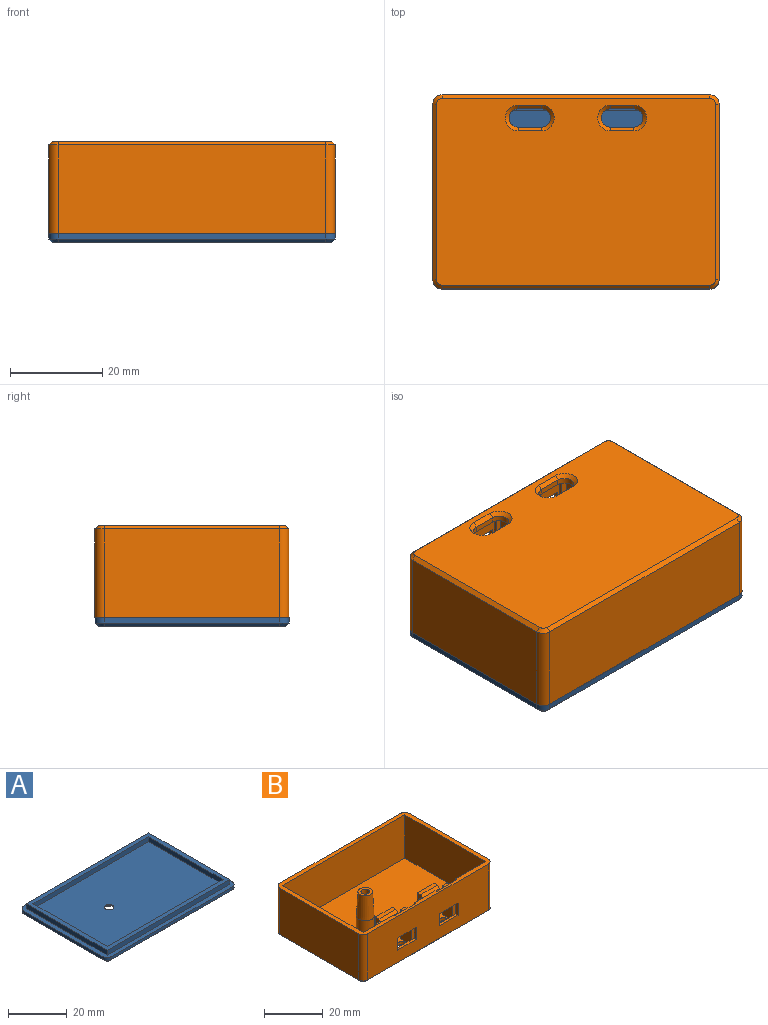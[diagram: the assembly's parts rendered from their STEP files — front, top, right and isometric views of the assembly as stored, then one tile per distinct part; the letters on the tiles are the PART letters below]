
ASSEMBLY  parts=2 mates=1
PART A: 30 faces, bbox 62x42x4 mm
  f0: plane 62x42mm, normal (0,0,1), area 323mm2, adj f1,f2,f3,f4,f6,f7,f8,f9
  f1: plane 38x1.2mm, normal (1,0,0), area 45.6mm2, adj f0,f6,f9,f25
  f2: plane 58x1.2mm, normal (0,1,0), area 69.6mm2, adj f0,f6,f7,f29
  f3: plane 38x1.2mm, normal (-1,0,0), area 45.6mm2, adj f0,f7,f8,f26
  f4: plane 58x1.2mm, normal (0,-1,0), area 69.6mm2, adj f0,f8,f9,f22
  f5: plane 60.4x40.4mm, normal (0,0,-1), area 2402.6mm2, adj f21,f22,f23,f24,f25,f26,f27,f28
  f6: cylinder r=2mm len=2mm, axis (0,0,1), area 3.8mm2, adj f0,f1,f2,f27
  f7: cylinder r=2mm len=2mm, axis (0,0,-1), area 3.8mm2, adj f0,f2,f3,f28
  f8: cylinder r=2mm len=2mm, axis (0,0,1), area 3.8mm2, adj f0,f3,f4,f24
  f9: cylinder r=2mm len=2mm, axis (0,0,-1), area 3.8mm2, adj f0,f1,f4,f23
  f10: plane 58.76x2mm, normal (0,-1,0), area 117.5mm2, adj f0,f11,f17,f18
  f11: plane 38.76x2mm, normal (1,0,0), area 77.5mm2, adj f0,f10,f12,f18
  f12: plane 58.76x2mm, normal (0,1,0), area 117.5mm2, adj f0,f11,f17,f18
  f13: plane 35.56x2mm, normal (-1,0,0), area 71.1mm2, adj f14,f16,f18,f19
  f14: plane 55.56x2mm, normal (0,1,0), area 111.1mm2, adj f13,f15,f18,f19
  f15: plane 35.56x2mm, normal (1,0,0), area 71.1mm2, adj f14,f16,f18,f19
  f16: plane 55.56x2mm, normal (0,-1,0), area 111.1mm2, adj f13,f15,f18,f19
  f17: plane 38.76x2mm, normal (-1,0,0), area 77.5mm2, adj f0,f10,f12,f18
  f18: plane 58.76x38.76mm, normal (0,0,1), area 301.8mm2, adj f10,f11,f12,f13,f14,f15,f16,f17
  f19: plane 55.56x35.56mm, normal (0,0,1), area 1967.7mm2, adj f13,f14,f15,f16,f20
  f20: cylinder r=1.6mm len=3.2mm, axis (0,0,1), area 2mm2, adj f19,f21
  f21: cone r=1.6mm half-angle=45deg, axis (0,0,-1), area 40mm2, adj f5,f20
  f22: plane 58x0.8mm, normal (0,-0.71,-0.71), area 65.6mm2, adj f4,f5,f23,f24
  f23: cone r=1.2mm half-angle=45deg, axis (0,0,1), area 2.8mm2, adj f5,f9,f22,f25
  f24: cone r=1.2mm half-angle=45deg, axis (0,0,1), area 2.8mm2, adj f5,f8,f22,f26
  f25: plane 38x0.8mm, normal (0.71,0,-0.71), area 43mm2, adj f1,f5,f23,f27
  f26: plane 38x0.8mm, normal (-0.71,0,-0.71), area 43mm2, adj f3,f5,f24,f28
  f27: cone r=1.2mm half-angle=45deg, axis (0,0,1), area 2.8mm2, adj f5,f6,f25,f29
  f28: cone r=1.2mm half-angle=45deg, axis (0,0,1), area 2.8mm2, adj f5,f7,f26,f29
  f29: plane 58x0.8mm, normal (0,0.71,-0.71), area 65.6mm2, adj f2,f5,f27,f28
PART B: 96 faces, bbox 62x42x20 mm
  f0: plane 10.1x8mm, normal (0,-1,0), area 80.8mm2, adj f20,f55,f58,f68
  f1: plane 10.1x8mm, normal (0,-1,0), area 80.8mm2, adj f20,f61,f63,f66
  f2: plane 12x5mm, normal (1,0,0), area 60mm2, adj f20,f26,f60,f62
  f3: plane 12x5mm, normal (-1,0,0), area 60mm2, adj f9,f20,f64,f65
  f4: plane 12x5mm, normal (1,0,0), area 60mm2, adj f20,f28,f54,f56
  f5: plane 12x5mm, normal (-1,0,0), area 60mm2, adj f14,f20,f57,f59
  f6: plane 12x5mm, normal (1,0,0), area 60mm2, adj f9,f20,f64,f65
  f7: plane 18x0.6mm, normal (1,0,0), area 10.8mm2, adj f18,f20,f21,f78
  f8: plane 18x0.6mm, normal (-1,0,0), area 10.8mm2, adj f18,f20,f21,f79
  f9: plane 5x2mm, normal (0,0,1), area 10mm2, adj f3,f6,f64,f65
  f10: plane 8x1.6mm, normal (0,0,1), area 12.8mm2, adj f61,f63,f71,f72
  f11: plane 12x5mm, normal (1,0,0), area 60mm2, adj f14,f20,f57,f59
  f12: plane 18x0.6mm, normal (1,0,0), area 10.8mm2, adj f17,f20,f21,f79
  f13: plane 18x0.6mm, normal (-1,0,0), area 10.8mm2, adj f17,f20,f21,f77
  f14: plane 5x2mm, normal (0,0,1), area 10mm2, adj f5,f11,f57,f59
  f15: plane 8x1.6mm, normal (0,0,1), area 12.8mm2, adj f55,f58,f70,f73
  f16: plane 58x19.2mm, normal (0,-1,0), area 1023.6mm2, adj f21,f37,f38,f39,f40,f41,f42,f43
  f17: plane 18x10mm, normal (0,1,0), area 135mm2, adj f12,f13,f20,f21,f41,f42,f43,f44
  f18: plane 18x10mm, normal (0,1,0), area 135mm2, adj f7,f8,f20,f21,f37,f38,f39,f40
  f19: plane 60.4x40.4mm, normal (0,0,-1), area 2333.7mm2, adj f80,f81,f82,f83,f84,f85,f86,f87
  f20: plane 58.8x39.4mm, normal (0,0,1), area 2118.4mm2, adj f0,f1,f2,f3,f4,f5,f6,f7
  f21: plane 62x42mm, normal (0,0,1), area 307.1mm2, adj f7,f8,f12,f13,f16,f17,f18,f22
  f22: plane 38x19.2mm, normal (1,0,0), area 729.6mm2, adj f21,f50,f51,f80
  f23: plane 58x19.2mm, normal (0,1,0), area 1113.6mm2, adj f21,f51,f52,f84
  f24: plane 38x19.2mm, normal (-1,0,0), area 729.6mm2, adj f21,f52,f53,f87
  f25: plane 12x5mm, normal (-1,0,0), area 60mm2, adj f20,f26,f60,f62
  f26: plane 5x2mm, normal (0,0,1), area 10mm2, adj f2,f25,f60,f62
  f27: plane 12x5mm, normal (-1,0,0), area 60mm2, adj f20,f28,f54,f56
  f28: plane 5x2mm, normal (0,0,1), area 10mm2, adj f4,f27,f54,f56
  f29: cylinder r=2mm len=4mm, axis (0,0,1), area 7.5mm2, adj f20,f30,f31,f94
  f30: plane 5x1.2mm, normal (0,-1,0), area 6mm2, adj f20,f29,f32,f92
  f31: plane 5x1.2mm, normal (0,1,0), area 6mm2, adj f20,f29,f32,f95
  f32: cylinder r=2mm len=4mm, axis (0,0,1), area 7.5mm2, adj f20,f30,f31,f93
  f33: plane 5x1.2mm, normal (0,-1,0), area 6mm2, adj f20,f34,f36,f88
  f34: cylinder r=2mm len=4mm, axis (0,0,1), area 7.5mm2, adj f20,f33,f35,f89
  f35: plane 5x1.2mm, normal (0,1,0), area 6mm2, adj f20,f34,f36,f91
  f36: cylinder r=2mm len=4mm, axis (0,0,1), area 7.5mm2, adj f20,f33,f35,f90
  f37: plane 9x1mm, normal (0,0,1), area 9mm2, adj f16,f18,f38,f40
  f38: plane 5x1mm, normal (1,0,0), area 5mm2, adj f16,f18,f37,f39
  f39: plane 9x1mm, normal (0,0,-1), area 9mm2, adj f16,f18,f38,f40
  f40: plane 5x1mm, normal (-1,0,0), area 5mm2, adj f16,f18,f37,f39
  f41: plane 5x1mm, normal (-1,0,0), area 5mm2, adj f16,f17,f42,f44
  f42: plane 9x1mm, normal (0,0,1), area 9mm2, adj f16,f17,f41,f43
  f43: plane 5x1mm, normal (1,0,0), area 5mm2, adj f16,f17,f42,f44
  f44: plane 9x1mm, normal (0,0,-1), area 9mm2, adj f16,f17,f41,f43
  f45: cylinder r=3mm len=6mm, axis (0,0,-1), area 94.2mm2, adj f20,f49
  f46: plane 5x5mm, normal (0,0,1), area 13mm2, adj f47,f49
  f47: cylinder r=1.45mm len=15mm, axis (0,0,1), area 136.7mm2, adj f46,f48
  f48: plane 2.9x2.9mm, normal (0,0,1), area 6.6mm2, adj f47
  f49: cone r=2.5mm half-angle=2.9deg, axis (0,0,-1), area 173mm2, adj f45,f46
  f50: cylinder r=2mm len=19.2mm, axis (0,0,1), area 60.3mm2, adj f16,f21,f22,f81
  f51: cylinder r=2mm len=19.2mm, axis (0,0,-1), area 60.3mm2, adj f21,f22,f23,f82
  f52: cylinder r=2mm len=19.2mm, axis (0,0,1), area 60.3mm2, adj f21,f23,f24,f86
  f53: cylinder r=2mm len=19.2mm, axis (0,0,-1), area 60.3mm2, adj f16,f21,f24,f85
  f54: plane 12x2mm, normal (0,1,0), area 24mm2, adj f4,f20,f27,f28
  f55: plane 12x3.2mm, normal (1,0,0), area 28.2mm2, adj f0,f15,f20,f68,f69,f70,f73
  f56: plane 12x2mm, normal (0,-1,0), area 24mm2, adj f4,f20,f27,f28
  f57: plane 12x2mm, normal (0,1,0), area 24mm2, adj f5,f11,f14,f20
  f58: plane 12x3.2mm, normal (-1,0,0), area 28.2mm2, adj f0,f15,f20,f68,f69,f70,f73
  f59: plane 12x2mm, normal (0,-1,0), area 24mm2, adj f5,f11,f14,f20
  f60: plane 12x2mm, normal (0,-1,0), area 24mm2, adj f2,f20,f25,f26
  f61: plane 12x3.2mm, normal (1,0,0), area 28.2mm2, adj f1,f10,f20,f66,f67,f71,f72
  f62: plane 12x2mm, normal (0,1,0), area 24mm2, adj f2,f20,f25,f26
  f63: plane 12x3.2mm, normal (-1,0,0), area 28.2mm2, adj f1,f10,f20,f66,f67,f71,f72
  f64: plane 12x2mm, normal (0,1,0), area 24mm2, adj f3,f6,f9,f20
  f65: plane 12x2mm, normal (0,-1,0), area 24mm2, adj f3,f6,f9,f20
  f66: plane 8x0.6mm, normal (0,0,-1), area 4.8mm2, adj f1,f61,f63,f67
  f67: plane 8x0.9mm, normal (0,-1,0), area 7.2mm2, adj f61,f63,f66,f71
  f68: plane 8x0.6mm, normal (0,0,-1), area 4.8mm2, adj f0,f55,f58,f69
  f69: plane 8x0.9mm, normal (0,-1,0), area 7.2mm2, adj f55,f58,f68,f70
  f70: plane 8x1mm, normal (0,-0.71,0.71), area 11.3mm2, adj f15,f55,f58,f69
  f71: plane 8x1mm, normal (0,-0.71,0.71), area 11.3mm2, adj f10,f61,f63,f67
  f72: plane 12x8mm, normal (0,1,0.05), area 96.1mm2, adj f10,f20,f61,f63
  f73: plane 12x8mm, normal (0,1,0.05), area 96.1mm2, adj f15,f20,f55,f58
  f74: plane 38.8x18mm, normal (1,0,0), area 698.4mm2, adj f20,f21,f75,f78
  f75: plane 58.8x18mm, normal (0,-1,0), area 1058.4mm2, adj f20,f21,f74,f76
  f76: plane 38.8x18mm, normal (-1,0,0), area 698.4mm2, adj f20,f21,f75,f77
  f77: plane 18x14.4mm, normal (0,1,0), area 259.2mm2, adj f13,f20,f21,f76
  f78: plane 18x14.4mm, normal (0,1,0), area 259.2mm2, adj f7,f20,f21,f74
  f79: plane 18x10mm, normal (0,1,0), area 180mm2, adj f8,f12,f20,f21
  f80: plane 38x0.8mm, normal (0.71,0,-0.71), area 43mm2, adj f19,f22,f81,f82
  f81: cone r=1.2mm half-angle=45deg, axis (0,0,1), area 2.8mm2, adj f19,f50,f80,f83
  f82: cone r=1.2mm half-angle=45deg, axis (0,0,1), area 2.8mm2, adj f19,f51,f80,f84
  f83: plane 58x0.8mm, normal (0,-0.71,-0.71), area 65.6mm2, adj f16,f19,f81,f85
  f84: plane 58x0.8mm, normal (0,0.71,-0.71), area 65.6mm2, adj f19,f23,f82,f86
  f85: cone r=1.2mm half-angle=45deg, axis (0,0,1), area 2.8mm2, adj f19,f53,f83,f87
  f86: cone r=1.2mm half-angle=45deg, axis (0,0,1), area 2.8mm2, adj f19,f52,f84,f87
  f87: plane 38x0.8mm, normal (-0.71,0,-0.71), area 43mm2, adj f19,f24,f85,f86
  f88: plane 5x0.8mm, normal (0,-0.71,-0.71), area 5.7mm2, adj f19,f33,f89,f90
  f89: cone r=2mm half-angle=45deg, axis (0,0,-1), area 8.5mm2, adj f19,f34,f88,f91
  f90: cone r=2mm half-angle=45deg, axis (0,0,-1), area 8.5mm2, adj f19,f36,f88,f91
  f91: plane 5x0.8mm, normal (0,0.71,-0.71), area 5.7mm2, adj f19,f35,f89,f90
  f92: plane 5x0.8mm, normal (0,-0.71,-0.71), area 5.7mm2, adj f19,f30,f93,f94
  f93: cone r=2.8mm half-angle=45deg, axis (0,0,-1), area 8.5mm2, adj f19,f32,f92,f95
  f94: cone r=2.8mm half-angle=45deg, axis (0,0,-1), area 8.5mm2, adj f19,f29,f92,f95
  f95: plane 5x0.8mm, normal (0,0.71,-0.71), area 5.7mm2, adj f19,f31,f93,f94
PLACE A t=(-0.14,0,0)mm
PLACE B rot(axis=(1,0,0),180deg) t=(-0.16,0.02,22)mm
MATE fastened A.f0 <-> B.f21  axis (0,0,1) through (29.24,-19.38,2)mm
